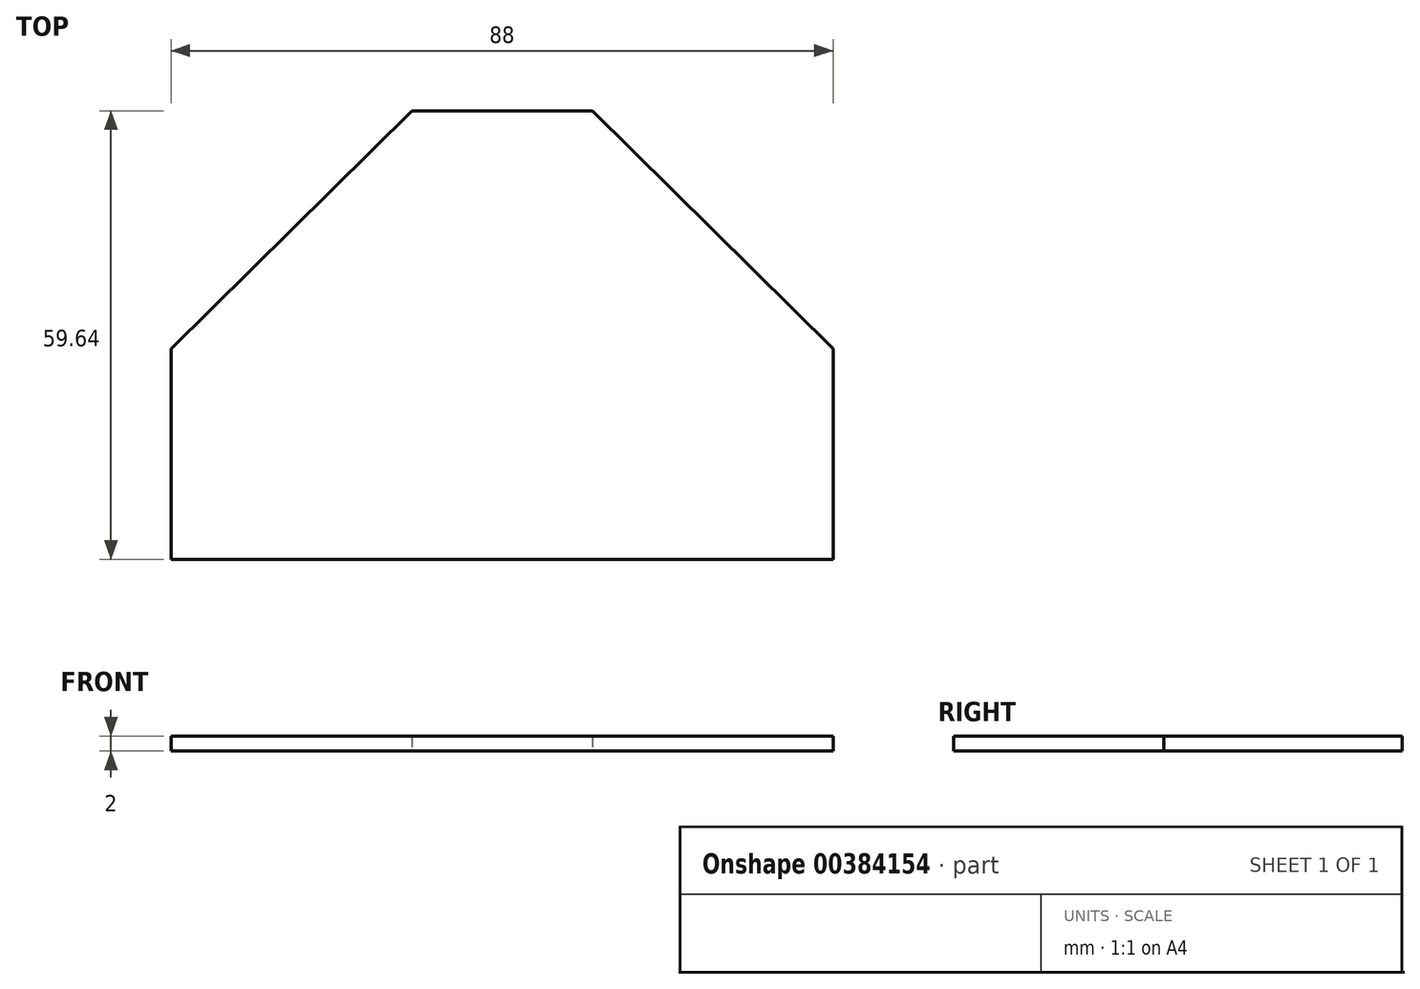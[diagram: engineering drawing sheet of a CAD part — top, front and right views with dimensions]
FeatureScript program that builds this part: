
annotation { "Feature Type Name" : "Feature", "Feature Type Description" : "" }
export const myFeature = defineFeature(function(context is Context, id is Id, definition is map)
    precondition{}
    {
        {
            var Q0;
            Q0=qCreatedBy(makeId("Top.planeOp"),FACE);
            var sketch = newSketch(context, id + "F0", { "sketchPlane" : qUnion([Q0])});
            skLineSegment(sketch, "E0", {"start": v(0, 0) * mm, "end": v(44, 0) * mm});
            skLineSegment(sketch, "E1", {"start": v(44, 0) * mm, "end": v(44, 28) * mm});
            skLineSegment(sketch, "E2", {"start": v(44, 28) * mm, "end": v(12, 59.64) * mm});
            skLineSegment(sketch, "E3", {"start": v(0, 59.64) * mm, "end": v(12, 59.64) * mm});
            skLineSegment(sketch, "E4", {"start": v(0, 0) * mm, "end": v(-44, 0) * mm});
            skLineSegment(sketch, "E5", {"start": v(-44, 0) * mm, "end": v(-44, 28) * mm});
            skLineSegment(sketch, "E6", {"start": v(-44, 28) * mm, "end": v(-12, 59.64) * mm});
            skLineSegment(sketch, "E7", {"start": v(0, 59.64) * mm, "end": v(-12, 59.64) * mm});
            skSolve(sketch);
        }
        {
            var Q0;
            Q0 = qSketchRegion(id + "F0", true);
            extrude(context, id + "F1", {"entities" : qUnion([Q0]), "depth" : 2 * mm});
        }
    });
